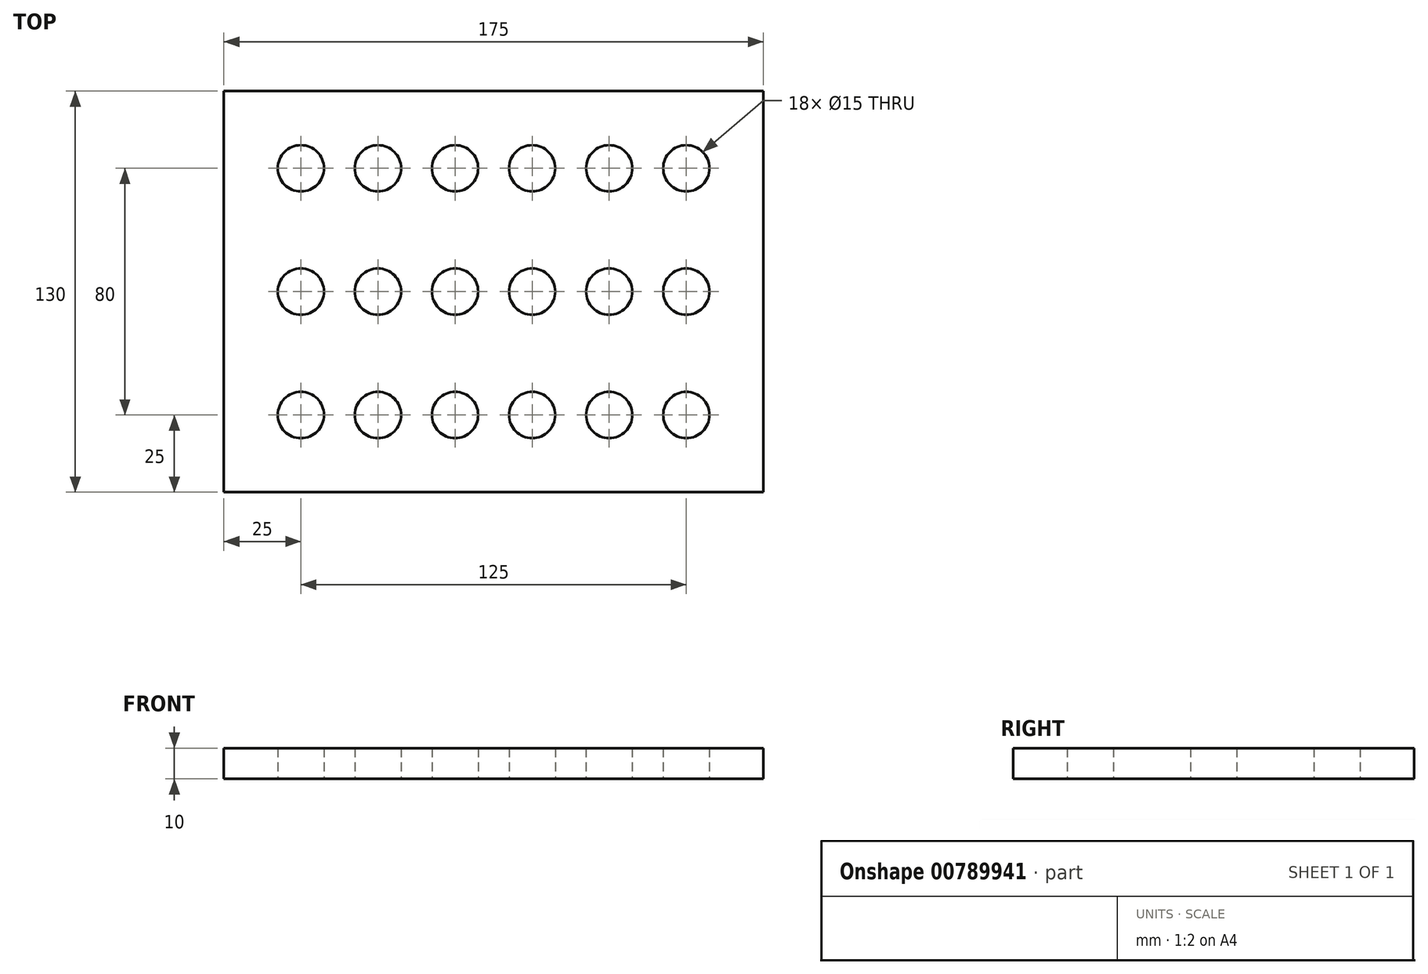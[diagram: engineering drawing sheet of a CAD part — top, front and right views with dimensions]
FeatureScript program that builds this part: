
annotation { "Feature Type Name" : "Feature", "Feature Type Description" : "" }
export const myFeature = defineFeature(function(context is Context, id is Id, definition is map)
    precondition{}
    {
        {
            var Q0;
            Q0=qCreatedBy(makeId("Top.planeOp"),FACE);
            var sketch = newSketch(context, id + "F0", { "sketchPlane" : qUnion([Q0])});
            skLineSegment(sketch, "E0.bottom", {"start": v(-87.5, 65) * mm, "end": v(87.5, 65) * mm});
            skLineSegment(sketch, "E0.top", {"start": v(-87.5, -65) * mm, "end": v(87.5, -65) * mm});
            skLineSegment(sketch, "E0.left", {"start": v(-87.5, 65) * mm, "end": v(-87.5, -65) * mm});
            skLineSegment(sketch, "E0.right", {"start": v(87.5, 65) * mm, "end": v(87.5, -65) * mm});
            skPoint(sketch, "E0.middle", {"position": v(0, 0) * mm});
            skCircle(sketch, "E1", {"center": v(-62.5, 40) * mm, "radius": 7.5 * mm});
            skCircle(sketch, "E2.0.1.0", {"center": v(-62.5, 0) * mm, "radius": 7.5 * mm});
            skCircle(sketch, "E2.0.2.0", {"center": v(-62.5, -40) * mm, "radius": 7.5 * mm});
            skCircle(sketch, "E2.1.0.0", {"center": v(-37.5, 40) * mm, "radius": 7.5 * mm});
            skCircle(sketch, "E2.1.1.0", {"center": v(-37.5, 0) * mm, "radius": 7.5 * mm});
            skCircle(sketch, "E2.1.2.0", {"center": v(-37.5, -40) * mm, "radius": 7.5 * mm});
            skCircle(sketch, "E2.2.0.0", {"center": v(-12.5, 40) * mm, "radius": 7.5 * mm});
            skCircle(sketch, "E2.2.1.0", {"center": v(-12.5, 0) * mm, "radius": 7.5 * mm});
            skCircle(sketch, "E2.2.2.0", {"center": v(-12.5, -40) * mm, "radius": 7.5 * mm});
            skCircle(sketch, "E2.3.0.0", {"center": v(12.5, 40) * mm, "radius": 7.5 * mm});
            skCircle(sketch, "E2.3.1.0", {"center": v(12.5, 0) * mm, "radius": 7.5 * mm});
            skCircle(sketch, "E2.3.2.0", {"center": v(12.5, -40) * mm, "radius": 7.5 * mm});
            skCircle(sketch, "E2.4.0.0", {"center": v(37.5, 40) * mm, "radius": 7.5 * mm});
            skCircle(sketch, "E2.4.1.0", {"center": v(37.5, 0) * mm, "radius": 7.5 * mm});
            skCircle(sketch, "E2.4.2.0", {"center": v(37.5, -40) * mm, "radius": 7.5 * mm});
            skCircle(sketch, "E2.5.0.0", {"center": v(62.5, 40) * mm, "radius": 7.5 * mm});
            skCircle(sketch, "E2.5.1.0", {"center": v(62.5, 0) * mm, "radius": 7.5 * mm});
            skCircle(sketch, "E2.5.2.0", {"center": v(62.5, -40) * mm, "radius": 7.5 * mm});
            skLineSegment(sketch, "E2.direction1", {"start": v(-62.5, 40) * mm, "end": v(-37.5, 40) * mm, "construction": true});
            skLineSegment(sketch, "E2.direction2", {"start": v(-62.5, 40) * mm, "end": v(-62.5, 0) * mm, "construction": true});
            skSolve(sketch);
        }
        {
            var Q0;
            Q0=makeQuery(id+"F0.imprint","IMPRINT",FACE,{"disambiguationData":[TD([[makeQuery(id+"F0.imprint","IMPRINT",EDGE,{"derivedFrom":sQuery(id+"F0.wireOp",EDGE,"E0.bottom")}),-1.0]])]});
            extrude(context, id + "F1", {"entities" : qUnion([Q0]), "depth" : 10 * mm, "offsetDistance" : 25 * mm});
        }
    });
